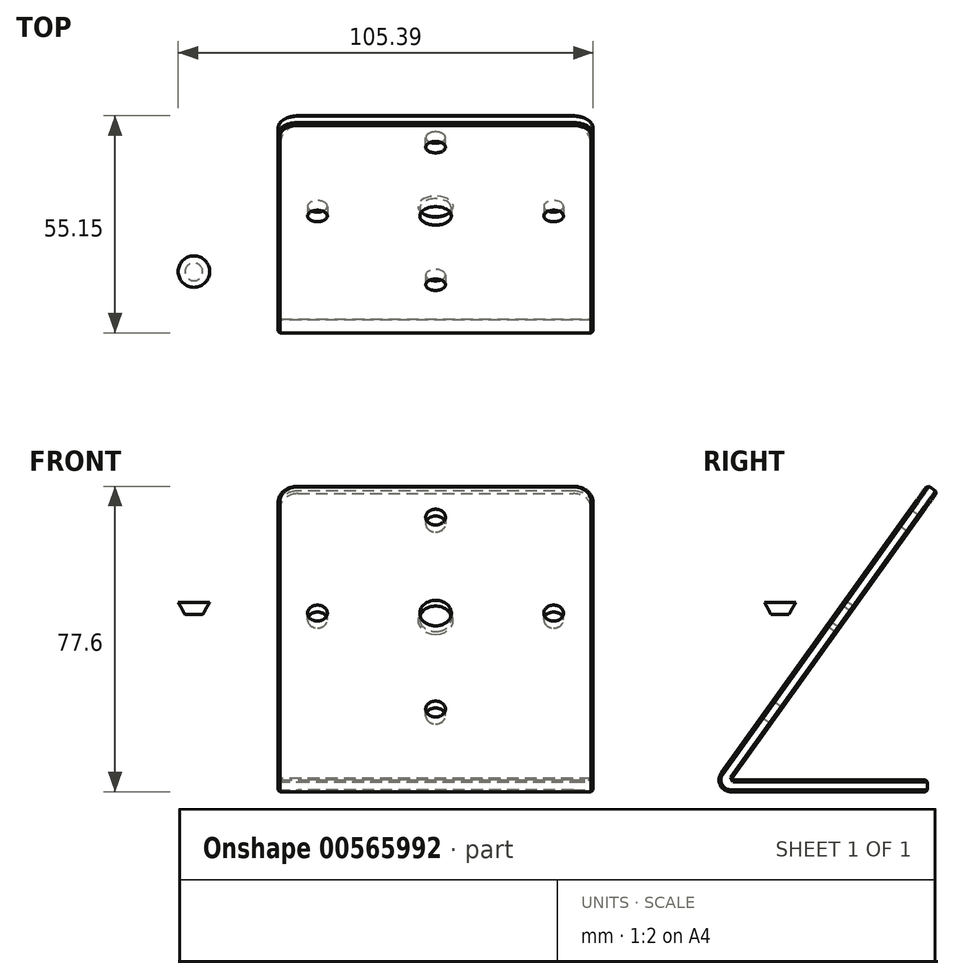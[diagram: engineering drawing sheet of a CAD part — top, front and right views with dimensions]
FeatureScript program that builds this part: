
annotation { "Feature Type Name" : "Feature", "Feature Type Description" : "" }
export const myFeature = defineFeature(function(context is Context, id is Id, definition is map)
    precondition{}
    {
        {
            var Q0;
            Q0=qCreatedBy(makeId("Right.planeOp"),FACE);
            var sketch = newSketch(context, id + "F0", { "sketchPlane" : qUnion([Q0])});
            skLineSegment(sketch, "E0", {"start": v(56.46, 29.8) * mm, "end": v(4.02, -43.34) * mm});
            skLineSegment(sketch, "E1", {"start": v(56.46, -48.1) * mm, "end": v(6.46, -48.1) * mm});
            skLineSegment(sketch, "E2", {"start": v(56.46, -48.1) * mm, "end": v(56.46, -45.1) * mm});
            skLineSegment(sketch, "E3", {"start": v(56.46, -45.1) * mm, "end": v(6.46, -45.1) * mm});
            skLineSegment(sketch, "E4", {"start": v(6.46, -45.1) * mm, "end": v(58.9, 28.05) * mm});
            skLineSegment(sketch, "E5", {"start": v(58.9, 28.05) * mm, "end": v(56.46, 29.8) * mm});
            skPoint(sketch, "E6.visualSharp", {"position": v(0.62, -48.1) * mm});
            skArc(sketch, "E6.filletArc", {"start": v(4.02, -43.34) * mm, "mid": v(3.8, -46.46) * mm, "end": v(6.46, -48.1) * mm});
            skSolve(sketch);
        }
        {
            var Q0;
            Q0=makeQuery(id+"F0.imprint","IMPRINT",FACE,{"disambiguationData":[TD([[makeQuery(id+"F0.imprint","IMPRINT",EDGE,{"derivedFrom":sQuery(id+"F0.wireOp",EDGE,"E0")}),1.0]])]});
            extrude(context, id + "F1", {"entities" : qUnion([Q0]), "depth" : 80 * mm, "offsetDistance" : 25 * mm, "symmetric" : true});
        }
        {
            var Q0;
            Q0=makeQuery(id+"F1.opExtrude","CAP_EDGE",EDGE,{"disambiguationData":[OSD([sQuery(id+"F0.wireOp",EDGE,"E5")])],"isStart":true});
            var Q1;
            Q1=makeQuery(id+"F1.opExtrude","CAP_EDGE",EDGE,{"disambiguationData":[OSD([sQuery(id+"F0.wireOp",EDGE,"E5")])],"isStart":false});
            var Q2;
            Q2=makeQuery(id+"F1.opExtrude","CAP_EDGE",EDGE,{"disambiguationData":[OSD([sQuery(id+"F0.wireOp",EDGE,"E2")])],"isStart":false});
            var Q3;
            Q3=makeQuery(id+"F1.opExtrude","CAP_EDGE",EDGE,{"disambiguationData":[OSD([sQuery(id+"F0.wireOp",EDGE,"E2")])],"isStart":true});
            fillet(context, id + "F2", {"entities" : qUnion([Q0, Q1, Q2, Q3]), "radius" : 5 * mm, "tangentPropagation" : true, "allowEdgeOverflow" : false});
        }
        {
            var Q0;
            Q0=makeQuery(id+"F1.opExtrude","SWEPT_FACE",FACE,{"disambiguationData":[OSD([sQuery(id+"F0.wireOp",EDGE,"E0")])]});
            var Q1;
            Q1=makeQuery(id+"F1.opExtrude","SWEPT_FACE",FACE,{"disambiguationData":[OSD([sQuery(id+"F0.wireOp",EDGE,"E4")])]});
            var Q2;
            Q2=makeQuery(id+"F1.opExtrude","SWEPT_FACE",FACE,{"disambiguationData":[OSD([sQuery(id+"F0.wireOp",EDGE,"E3")])]});
            chamfer(context, id + "F3", {"entities" : qUnion([Q0, Q1, Q2]), "width" : 0.5 * mm, "tangentPropagation" : true});
        }
        {
            var Q0;
            Q0=makeQuery(id+"F1.opExtrude","SWEPT_FACE",FACE,{"disambiguationData":[OSD([sQuery(id+"F0.wireOp",EDGE,"E0")])]});
            var sketch = newSketch(context, id + "F4", { "sketchPlane" : qUnion([Q0])});
            skCircle(sketch, "E7", {"center": v(0, 17.12) * mm, "radius": 4 * mm});
            skSolve(sketch);
        }
        {
            var Q0;
            Q0=makeQuery(id+"F4.imprint","IMPRINT",FACE,{"disambiguationData":[TD([[makeQuery(id+"F4.imprint","IMPRINT",EDGE,{"derivedFrom":sQuery(id+"F4.wireOp",EDGE,"E7")}),1.0]])]});
            extrude(context, id + "F5", {"entities" : qUnion([Q0]), "operationType" : NewBodyOperationType.REMOVE, "oppositeDirection" : true, "depth" : 25 * mm, "offsetDistance" : 25 * mm});
        }
        {
            var Q0;
            Q0=makeQuery(id+"F1.opExtrude","SWEPT_FACE",FACE,{"disambiguationData":[OSD([sQuery(id+"F0.wireOp",EDGE,"E0")])]});
            var sketch = newSketch(context, id + "F6", { "sketchPlane" : qUnion([Q0])});
            skCircle(sketch, "E8", {"center": v(0, 47.12) * mm, "radius": 1.25 * mm});
            skSolve(sketch);
        }
        {
            var Q0;
            Q0 = qSketchRegion(id + "F6", true);
            extrude(context, id + "F7", {"entities" : qUnion([Q0]), "operationType" : NewBodyOperationType.REMOVE, "oppositeDirection" : true, "depth" : 4 * mm, "offsetDistance" : 25 * mm});
        }
        {
            var Q0;
            Q0=makeQuery(id+"F6.imprint","IMPRINT",FACE,{"disambiguationData":[TD([[makeQuery(id+"F6.imprint","IMPRINT",EDGE,{"derivedFrom":sQuery(id+"F6.wireOp",EDGE,"E8")}),-1.0]])]});
            var sketch = newSketch(context, id + "F8", { "sketchPlane" : qUnion([Q0])});
            skPoint(sketch, "E9", {"position": v(0, 47.12) * mm});
            skPoint(sketch, "E10.1.0", {"position": v(-40.8, -23.56) * mm});
            skPoint(sketch, "E10.2.0", {"position": v(40.8, -23.56) * mm});
            skPoint(sketch, "E10.center", {"position": v(0, 0) * mm});
            skSolve(sketch);
        }
        {
            var Q0;
            Q0=sQuery(id+"F8.wireOp",VERTEX,"E9");
            var Q1;
            Q1=makeQuery(id+"F1.opExtrude","SWEPT_BODY",BODY,{"disambiguationData":[OSD([sQuery(id+"F0.wireOp",EDGE,"E0"),sQuery(id+"F0.wireOp",EDGE,"E1"),sQuery(id+"F0.wireOp",EDGE,"E2"),sQuery(id+"F0.wireOp",EDGE,"E3"),sQuery(id+"F0.wireOp",EDGE,"E4"),sQuery(id+"F0.wireOp",EDGE,"E5"),sQuery(id+"F0.wireOp",EDGE,"E6.filletArc")])]});
            hole(context, id + "F9", {"style" : HoleStyle.SIMPLE, "endStyle" : HoleEndStyle.BLIND, "holeDiameter" : 5 * mm, "holeDepth" : 4 * mm, "isTappedThrough" : true, "tappedDepth" : 12 * mm, "tapClearance" : 3, "locations" : qUnion([Q0]), "scope" : qUnion([Q1]), "startStyle" : HoleStartStyle.PART});
        }
        {
            var Q0;
            Q0=makeQuery(id+"F1.opExtrude","SWEPT_FACE",FACE,{"disambiguationData":[OSD([sQuery(id+"F0.wireOp",EDGE,"E0")])]});
            var sketch = newSketch(context, id + "F10", { "sketchPlane" : qUnion([Q0])});
            skCircle(sketch, "E11", {"center": v(-30, 17.12) * mm, "radius": 2.5 * mm});
            skCircle(sketch, "E12", {"center": v(30, 17.12) * mm, "radius": 2.5 * mm});
            skCircle(sketch, "E13", {"center": v(0, -12.88) * mm, "radius": 2.5 * mm});
            skSolve(sketch);
        }
        {
            var Q0;
            Q0 = qSketchRegion(id + "F10", true);
            extrude(context, id + "F11", {"entities" : qUnion([Q0]), "operationType" : NewBodyOperationType.REMOVE, "oppositeDirection" : true, "depth" : 5 * mm, "offsetDistance" : 25 * mm});
        }
        {
            var Q0;
            Q0=qCreatedBy(makeId("Top.planeOp"),FACE);
            var sketch = newSketch(context, id + "F12", { "sketchPlane" : qUnion([Q0])});
            skCircle(sketch, "E14", {"center": v(-61.4, 19) * mm, "radius": 4 * mm});
            skSolve(sketch);
        }
        {
            var Q0;
            Q0=qCreatedBy(makeId("Top.planeOp"),FACE);
            cPlane(context, id + "F13", {"entities" : qUnion([Q0]), "cplaneType" : CPlaneType.OFFSET, "offset" : 3 * mm, "oppositeDirection" : true, "width" : 150 * mm, "height" : 150 * mm});
        }
        {
            var Q0;
            Q0=qCreatedBy(id+"F13.planeOp",FACE);
            var sketch = newSketch(context, id + "F14", { "sketchPlane" : qUnion([Q0])});
            skCircle(sketch, "E15", {"center": v(-61.4, 18.95) * mm, "radius": 2.27 * mm});
            skSolve(sketch);
        }
        {
            var Q0;
            Q0=makeQuery(id+"F12.imprint","IMPRINT",FACE,{"disambiguationData":[TD([[makeQuery(id+"F12.imprint","IMPRINT",EDGE,{"derivedFrom":sQuery(id+"F12.wireOp",EDGE,"E14")}),1.0]])]});
            var Q1;
            Q1=makeQuery(id+"F14.imprint","IMPRINT",FACE,{"disambiguationData":[TD([[makeQuery(id+"F14.imprint","IMPRINT",EDGE,{"derivedFrom":sQuery(id+"F14.wireOp",EDGE,"E15")}),1.0]])]});
            loft(context, id + "F15", {"sheetProfilesArray" : [{ "sheetProfileEntities" : qUnion([Q0]) }, { "sheetProfileEntities" : qUnion([Q1]) }]});
        }
        {
            var Q0;
            Q0=makeQuery(id+"F5.boolean.opBoolean","COPY",EDGE,{"derivedFrom":makeQuery(id+"F5.opExtrude","CAP_EDGE",EDGE,{"disambiguationData":[OSD([sQuery(id+"F4.wireOp",EDGE,"E7")])],"isStart":true})});
            var Q1;
            Q1=makeQuery(id+"F5.boolean.opBoolean","INTERSECT",EDGE,{"derivedFrom":[makeQuery(id+"F1.opExtrude","SWEPT_FACE",FACE,{"disambiguationData":[OSD([sQuery(id+"F0.wireOp",EDGE,"E4")])]}),makeQuery(id+"F5.opExtrude","SWEPT_FACE",FACE,{"disambiguationData":[OSD([sQuery(id+"F4.wireOp",EDGE,"E7")])]})]});
            chamfer(context, id + "F16", {"entities" : qUnion([Q0, Q1]), "width" : 0.5 * mm, "tangentPropagation" : true});
        }
    });
